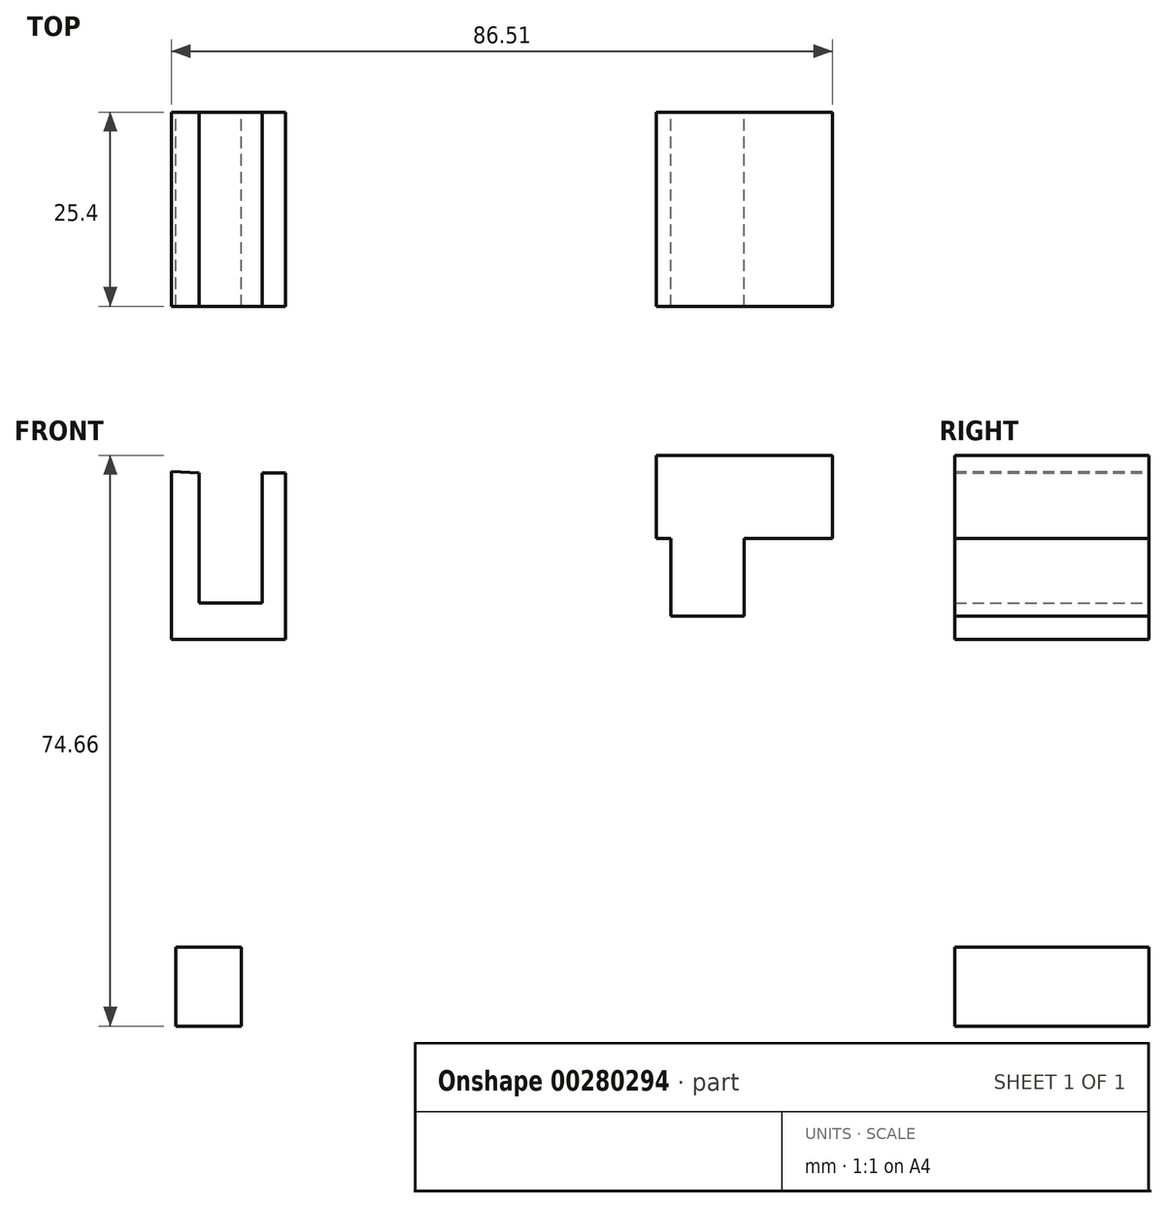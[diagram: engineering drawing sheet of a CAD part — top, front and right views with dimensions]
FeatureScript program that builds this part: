
annotation { "Feature Type Name" : "Feature", "Feature Type Description" : "" }
export const myFeature = defineFeature(function(context is Context, id is Id, definition is map)
    precondition{}
    {
        {
            var Q0;
            Q0=qCreatedBy(makeId("Front.planeOp"),FACE);
            var sketch = newSketch(context, id + "F0", { "sketchPlane" : qUnion([Q0])});
            skLineSegment(sketch, "E0", {"start": v(-57.48, 41.63) * mm, "end": v(-57.48, 19.67) * mm});
            skLineSegment(sketch, "E1", {"start": v(-57.48, 19.67) * mm, "end": v(-42.58, 19.67) * mm});
            skLineSegment(sketch, "E2", {"start": v(-42.58, 19.67) * mm, "end": v(-42.58, 41.44) * mm});
            skLineSegment(sketch, "E3", {"start": v(-42.58, 41.44) * mm, "end": v(-45.64, 41.44) * mm});
            skLineSegment(sketch, "E4", {"start": v(-45.64, 41.44) * mm, "end": v(-45.64, 24.44) * mm});
            skLineSegment(sketch, "E5", {"start": v(-45.64, 24.44) * mm, "end": v(-53.85, 24.44) * mm});
            skLineSegment(sketch, "E6", {"start": v(-53.85, 24.44) * mm, "end": v(-53.85, 41.44) * mm});
            skLineSegment(sketch, "E7", {"start": v(-53.85, 41.44) * mm, "end": v(-57.48, 41.63) * mm});
            skSolve(sketch);
        }
        {
            var Q0;
            Q0 = qSketchRegion(id + "F0", true);
            extrude(context, id + "F1", {"entities" : qUnion([Q0]), "depth" : 25.4 * mm});
        }
        {
            var Q0;
            Q0=qCreatedBy(makeId("Front.planeOp"),FACE);
            var sketch = newSketch(context, id + "F2", { "sketchPlane" : qUnion([Q0])});
            skLineSegment(sketch, "E8.bottom", {"start": v(5.92, 43.73) * mm, "end": v(29.03, 43.73) * mm});
            skLineSegment(sketch, "E8.top", {"start": v(5.92, 32.84) * mm, "end": v(29.03, 32.84) * mm});
            skLineSegment(sketch, "E8.left", {"start": v(5.92, 43.73) * mm, "end": v(5.92, 32.84) * mm});
            skLineSegment(sketch, "E8.right", {"start": v(29.03, 43.73) * mm, "end": v(29.03, 32.84) * mm});
            skPoint(sketch, "E9.oppositeSnap0", {"position": v(17.47, 32.84) * mm});
            skLineSegment(sketch, "E9.bottom", {"start": v(7.83, 32.84) * mm, "end": v(17.47, 32.84) * mm});
            skLineSegment(sketch, "E9.top", {"start": v(7.83, 22.72) * mm, "end": v(17.47, 22.72) * mm});
            skLineSegment(sketch, "E9.left", {"start": v(7.83, 32.84) * mm, "end": v(7.83, 22.72) * mm});
            skLineSegment(sketch, "E9.right", {"start": v(17.47, 32.84) * mm, "end": v(17.47, 22.72) * mm});
            skSolve(sketch);
        }
        {
            var Q0;
            Q0 = qSketchRegion(id + "F2", true);
            extrude(context, id + "F3", {"entities" : qUnion([Q0]), "depth" : 25.4 * mm});
        }
        {
            var Q0;
            Q0=qCreatedBy(makeId("Front.planeOp"),FACE);
            var sketch = newSketch(context, id + "F4", { "sketchPlane" : qUnion([Q0])});
            skLineSegment(sketch, "E10.bottom", {"start": v(-56.9, -20.62) * mm, "end": v(-30.17, -20.62) * mm});
            skLineSegment(sketch, "E10.top", {"start": v(-56.9, -49.84) * mm, "end": v(-30.17, -49.84) * mm});
            skLineSegment(sketch, "E10.left", {"start": v(-56.9, -20.62) * mm, "end": v(-56.9, -49.84) * mm});
            skLineSegment(sketch, "E10.right", {"start": v(-30.17, -20.62) * mm, "end": v(-30.17, -49.84) * mm});
            skLineSegment(sketch, "E11", {"start": v(-48.31, -20.62) * mm, "end": v(-48.31, -30.93) * mm});
            skLineSegment(sketch, "E12", {"start": v(-48.31, -30.93) * mm, "end": v(-56.9, -30.93) * mm});
            skSolve(sketch);
        }
        {
            var Q0;
            {var subQ3=sQuery(id+"F4.wireOp",EDGE,"E11");Q0=makeQuery(id+"F4.imprint","IMPRINT",FACE,{"disambiguationData":[TD([[makeQuery(id+"F4.imprint","IMPRINT",EDGE,{"derivedFrom":subQ3}),-1.0]])]});}
            extrude(context, id + "F5", {"entities" : qUnion([Q0]), "depth" : 25.4 * mm});
        }
    });
